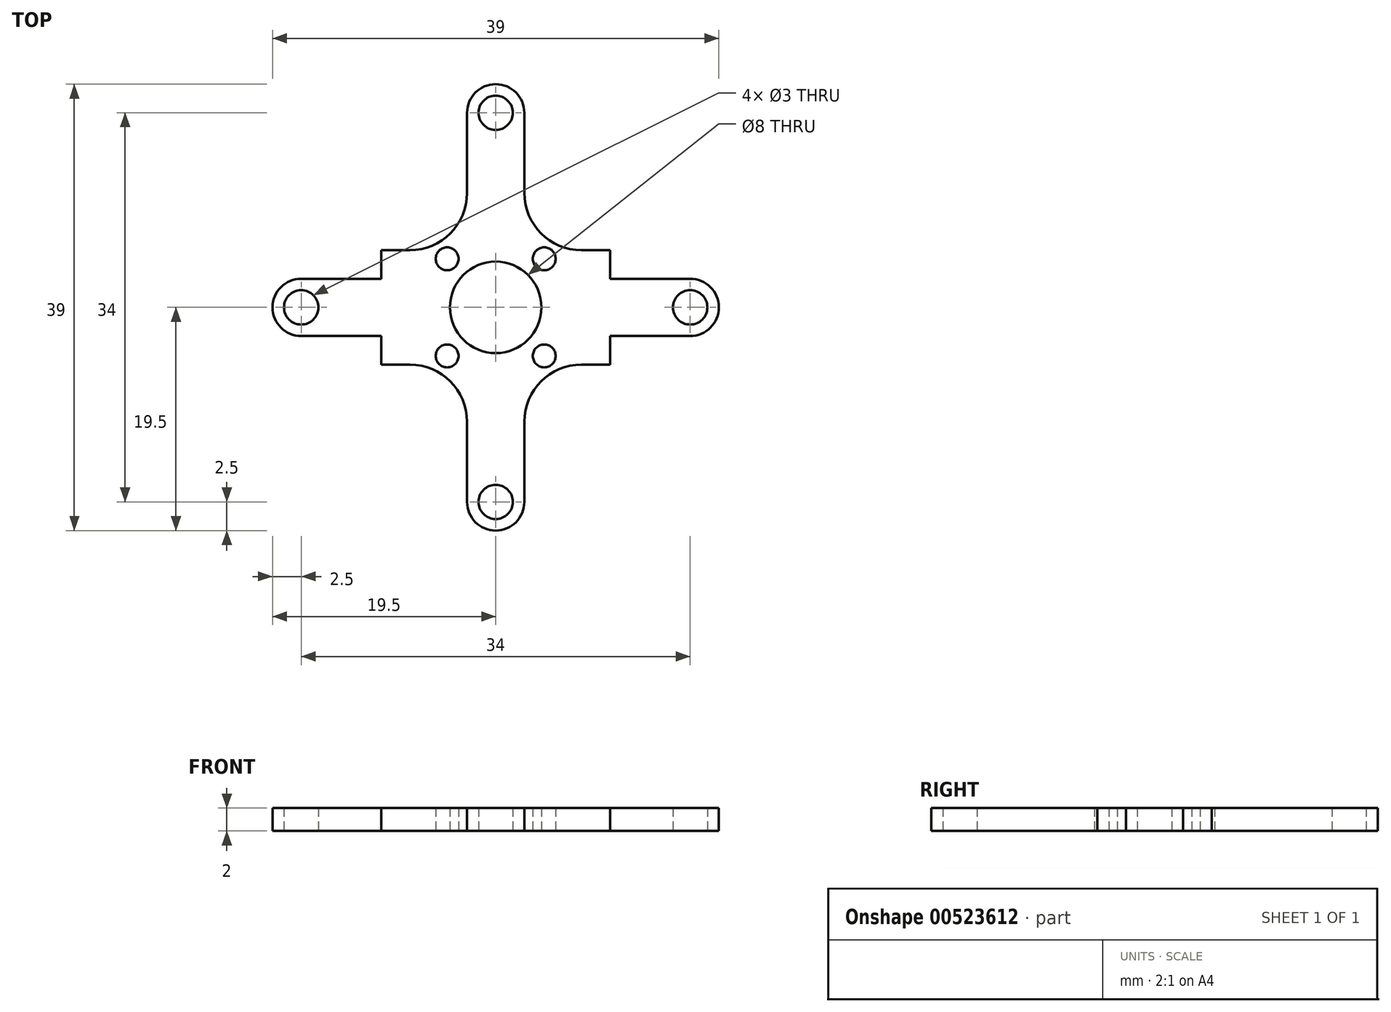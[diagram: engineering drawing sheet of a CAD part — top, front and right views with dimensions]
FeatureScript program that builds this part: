
annotation { "Feature Type Name" : "Feature", "Feature Type Description" : "" }
export const myFeature = defineFeature(function(context is Context, id is Id, definition is map)
    precondition{}
    {
        {
            var Q0;
            Q0=qCreatedBy(makeId("Top.planeOp"),FACE);
            var sketch = newSketch(context, id + "F0", { "sketchPlane" : qUnion([Q0])});
            skLineSegment(sketch, "E0.bottom", {"start": v(-2.5, 17) * mm, "end": v(2.5, 17) * mm});
            skLineSegment(sketch, "E0.top", {"start": v(-2.5, -17) * mm, "end": v(2.5, -17) * mm});
            skLineSegment(sketch, "E0.left", {"start": v(-2.5, 17) * mm, "end": v(-2.5, 10) * mm});
            skLineSegment(sketch, "E0.right", {"start": v(2.5, 17) * mm, "end": v(2.5, 10) * mm});
            skPoint(sketch, "E0.middle", {"position": v(0, 0) * mm});
            skCircle(sketch, "E1", {"center": v(0, 17) * mm, "radius": 2.5 * mm});
            skCircle(sketch, "E2", {"center": v(0, 17) * mm, "radius": 1.5 * mm});
            skCircle(sketch, "E3", {"center": v(0, -17) * mm, "radius": 1.5 * mm});
            skCircle(sketch, "E4", {"center": v(0, -17) * mm, "radius": 2.5 * mm});
            skLineSegment(sketch, "E5.bottom", {"start": v(-10, 5) * mm, "end": v(-7.5, 5) * mm});
            skLineSegment(sketch, "E5.top", {"start": v(-10, -5) * mm, "end": v(-7.5, -5) * mm});
            skLineSegment(sketch, "E5.left", {"start": v(-10, 5) * mm, "end": v(-10, -5) * mm});
            skLineSegment(sketch, "E5.right", {"start": v(10, 5) * mm, "end": v(10, -5) * mm});
            skLineSegment(sketch, "E6.bottom", {"start": v(17, -2.5) * mm, "end": v(-17, -2.5) * mm});
            skLineSegment(sketch, "E6.top", {"start": v(17, 2.5) * mm, "end": v(-17, 2.5) * mm});
            skLineSegment(sketch, "E6.left", {"start": v(17, -2.5) * mm, "end": v(17, 2.5) * mm});
            skLineSegment(sketch, "E6.right", {"start": v(-17, -2.5) * mm, "end": v(-17, 2.5) * mm});
            skCircle(sketch, "E7", {"center": v(-17, 0) * mm, "radius": 1.5 * mm});
            skCircle(sketch, "E8", {"center": v(-17, 0) * mm, "radius": 2.5 * mm});
            skCircle(sketch, "E9", {"center": v(17, 0) * mm, "radius": 2.5 * mm});
            skCircle(sketch, "E10", {"center": v(17, 0) * mm, "radius": 1.5 * mm});
            skCircle(sketch, "E11", {"center": v(0, 0) * mm, "radius": 4 * mm});
            skCircle(sketch, "E12", {"center": v(-4.24, 4.24) * mm, "radius": 1 * mm});
            skLineSegment(sketch, "E13", {"start": v(-4.24, 4.24) * mm, "end": v(0, 0) * mm});
            skCircle(sketch, "E14.1.0", {"center": v(-4.24, -4.24) * mm, "radius": 1 * mm});
            skCircle(sketch, "E14.2.0", {"center": v(4.24, -4.24) * mm, "radius": 1 * mm});
            skCircle(sketch, "E14.3.0", {"center": v(4.24, 4.24) * mm, "radius": 1 * mm});
            skLineSegment(sketch, "E15.trimOffspring", {"start": v(7.5, 5) * mm, "end": v(10, 5) * mm});
            skLineSegment(sketch, "E16.trimOffspring", {"start": v(7.5, -5) * mm, "end": v(10, -5) * mm});
            skLineSegment(sketch, "E17.trimOffspring", {"start": v(2.5, 3.12) * mm, "end": v(2.5, -3.12) * mm});
            skLineSegment(sketch, "E18.trimOffspring", {"start": v(-2.5, 3.12) * mm, "end": v(-2.5, -3.12) * mm});
            skLineSegment(sketch, "E19.trimOffspring", {"start": v(-2.5, -10) * mm, "end": v(-2.5, -17) * mm});
            skLineSegment(sketch, "E20.trimOffspring", {"start": v(2.5, -10) * mm, "end": v(2.5, -17) * mm});
            skPoint(sketch, "E21.visualSharp", {"position": v(-2.5, -5) * mm});
            skArc(sketch, "E21.filletArc", {"start": v(-2.5, -10) * mm, "mid": v(-3.96, -6.46) * mm, "end": v(-7.5, -5) * mm});
            skPoint(sketch, "E22.visualSharp", {"position": v(2.5, -5) * mm});
            skArc(sketch, "E22.filletArc", {"start": v(7.5, -5) * mm, "mid": v(3.96, -6.46) * mm, "end": v(2.5, -10) * mm});
            skPoint(sketch, "E23.visualSharp", {"position": v(2.5, 5) * mm});
            skArc(sketch, "E23.filletArc", {"start": v(2.5, 10) * mm, "mid": v(3.96, 6.46) * mm, "end": v(7.5, 5) * mm});
            skPoint(sketch, "E24.visualSharp", {"position": v(-2.5, 5) * mm});
            skArc(sketch, "E24.filletArc", {"start": v(-7.5, 5) * mm, "mid": v(-3.96, 6.46) * mm, "end": v(-2.5, 10) * mm});
            skSolve(sketch);
        }
        {
            var Q0;
            Q0 = qSketchRegion(id + "F0", true);
            extrude(context, id + "F1", {"entities" : qUnion([Q0]), "depth" : 2 * mm, "offsetDistance" : 25 * mm});
        }
    });
